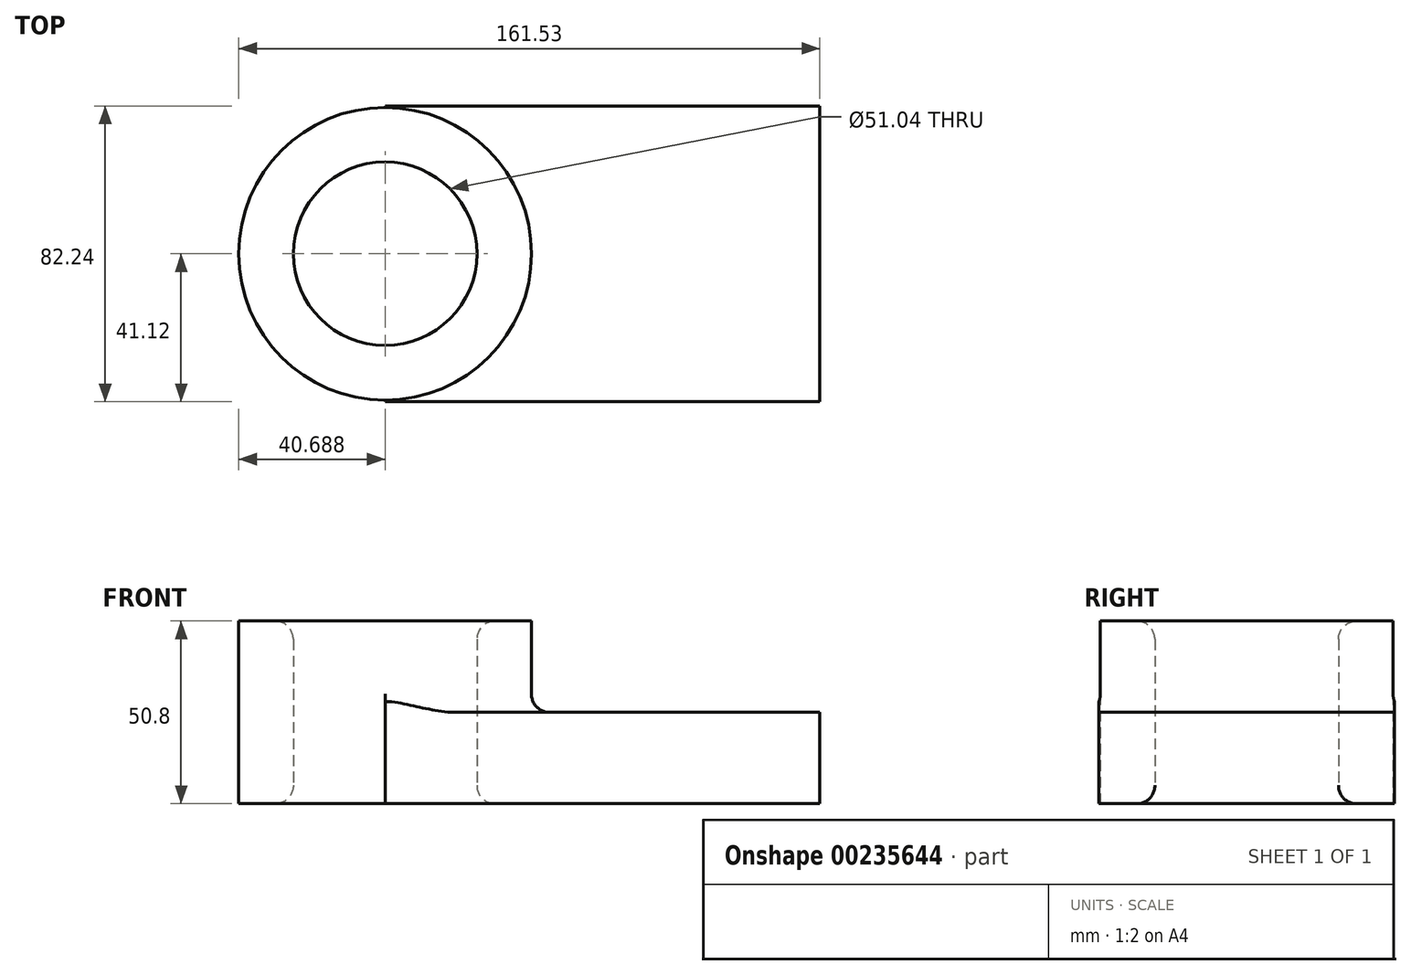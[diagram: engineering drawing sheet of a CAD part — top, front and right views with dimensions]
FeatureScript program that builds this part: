
annotation { "Feature Type Name" : "Feature", "Feature Type Description" : "" }
export const myFeature = defineFeature(function(context is Context, id is Id, definition is map)
    precondition{}
    {
        {
            var Q0;
            Q0=qCreatedBy(makeId("Top.planeOp"),FACE);
            var sketch = newSketch(context, id + "F0", { "sketchPlane" : qUnion([Q0])});
            skLineSegment(sketch, "E0.bottom", {"start": v(-60.42, 41.12) * mm, "end": v(60.42, 41.12) * mm});
            skLineSegment(sketch, "E0.top", {"start": v(-60.42, -41.12) * mm, "end": v(60.42, -41.12) * mm});
            skLineSegment(sketch, "E0.left", {"start": v(-60.42, 41.12) * mm, "end": v(-60.42, -41.12) * mm});
            skLineSegment(sketch, "E0.right", {"start": v(60.42, 41.12) * mm, "end": v(60.42, -41.12) * mm});
            skPoint(sketch, "E0.middle", {"position": v(0, 0) * mm});
            skCircle(sketch, "E1", {"center": v(-60.42, 0) * mm, "radius": 40.69 * mm});
            skCircle(sketch, "E2", {"center": v(-60.42, 0) * mm, "radius": 25.52 * mm});
            skSolve(sketch);
        }
        {
            var Q0;
            Q0 = qSketchRegion(id + "F0", true);
            extrude(context, id + "F1", {"entities" : qUnion([Q0]), "depth" : 25.4 * mm});
        }
        {
            var Q0;
            {var subQ0=sQuery(id+"F0.wireOp",EDGE,"E1");var subQ1=sQuery(id+"F0.wireOp",EDGE,"E0.left");var subQ2=makeQuery(id+"F0.imprint","INTERSECT",VERTEX,{"disambiguationData":[OD(0.0)],"derivedFrom":[subQ1,subQ0]});Q0=makeQuery(id+"F0.imprint","IMPRINT",FACE,{"disambiguationData":[TD([[makeQuery(id+"F0.imprint","IMPRINT",EDGE,{"disambiguationData":[TD([[subQ2,-1.0]])],"derivedFrom":subQ1}),-1.0]])]});}
            var Q1;
            {var subQ0=sQuery(id+"F0.wireOp",EDGE,"E1");var subQ1=sQuery(id+"F0.wireOp",EDGE,"E0.left");var subQ2=makeQuery(id+"F0.imprint","INTERSECT",VERTEX,{"disambiguationData":[OD(0.0)],"derivedFrom":[subQ1,subQ0]});Q1=makeQuery(id+"F0.imprint","IMPRINT",FACE,{"disambiguationData":[TD([[makeQuery(id+"F0.imprint","IMPRINT",EDGE,{"disambiguationData":[TD([[subQ2,-1.0]])],"derivedFrom":subQ1}),1.0]])]});}
            extrude(context, id + "F2", {"entities" : qUnion([Q0, Q1]), "operationType" : NewBodyOperationType.ADD, "depth" : 50.8 * mm});
        }
        {
            var Q0;
            {var subQ0=sQuery(id+"F0.wireOp",EDGE,"E1");Q0=makeQuery(id+"F2.boolean.opBoolean","INTERSECT",EDGE,{"derivedFrom":[makeQuery(id+"F1.opExtrude","CAP_FACE",FACE,{"disambiguationData":[OSD([sQuery(id+"F0.wireOp",EDGE,"E0.bottom"),sQuery(id+"F0.wireOp",EDGE,"E0.top"),sQuery(id+"F0.wireOp",EDGE,"E0.left"),sQuery(id+"F0.wireOp",EDGE,"E0.right"),subQ0,sQuery(id+"F0.wireOp",EDGE,"E2")])],"isStart":false}),makeQuery(id+"F2.opExtrude","SWEPT_FACE",FACE,{"disambiguationData":[OSD([subQ0])]})]});}
            fillet(context, id + "F3", {"entities" : qUnion([Q0]), "radius" : 5.08 * mm, "tangentPropagation" : true, "allowEdgeOverflow" : false});
        }
        {
            var Q0;
            Q0=makeQuery(id+"F2.opExtrude","CAP_EDGE",EDGE,{"disambiguationData":[OSD([sQuery(id+"F0.wireOp",EDGE,"E2")])],"isStart":false});
            var Q1;
            {var subQ0=sQuery(id+"F0.wireOp",EDGE,"E2");Q1=makeQuery(id+"F2.boolean.opBoolean","MERGE",FACE,{"derivedFrom":[makeQuery(id+"F1.opExtrude","SWEPT_FACE",FACE,{"disambiguationData":[OSD([subQ0])]}),makeQuery(id+"F2.opExtrude","SWEPT_FACE",FACE,{"disambiguationData":[OSD([subQ0])]})]});}
            fillet(context, id + "F4", {"entities" : qUnion([Q0, Q1]), "radius" : 5.08 * mm, "tangentPropagation" : true, "allowEdgeOverflow" : false});
        }
    });
